# Revit family: RM-23
name_source: partatom
category: Plumbing Fixtures
revit_build: Autodesk Revit 2014 (Build: 20130308_1515(x64)
units: mm (PartAtom-declared; Revit-internal decimal feet)

## types (1)
- RM-23
    Brass Chromed = Brass
    Certification = http://helvex.com
    Data Sheet = http://helvex.com
    Description = Slide Height Shower With Antiscale System
    Features = Shower Medium And High Pressure; Semi-Recessed Fixture; Setting Kit Included; Adjustable Height Mechanism Fixed Jet; Length Hose 59" (1,5 m); With Antiscale System
    Inlet Threads = ½" - 14 NPT
    Instructive = http://helvex.com
    Manufacturer = HELVEX
    Max. Water Flow = 85.3 gal/min
    Max. Working Pressure = 2.6 psi
    Min. Water Flow = 14.2 gal/min
    Min. Working Pressure = 0.7 psi
    Model = RM-23
    Plastic Showerhead = Plastic
    Total Depth = 2"
    Total Length = 23"
    Total Width = 10"
    Type Comments = Hand Showers
    URL = http://helvex.com

## geometry (parser evidence)
native form markers: Sweep x1
no freeform markers — native parametric forms only
